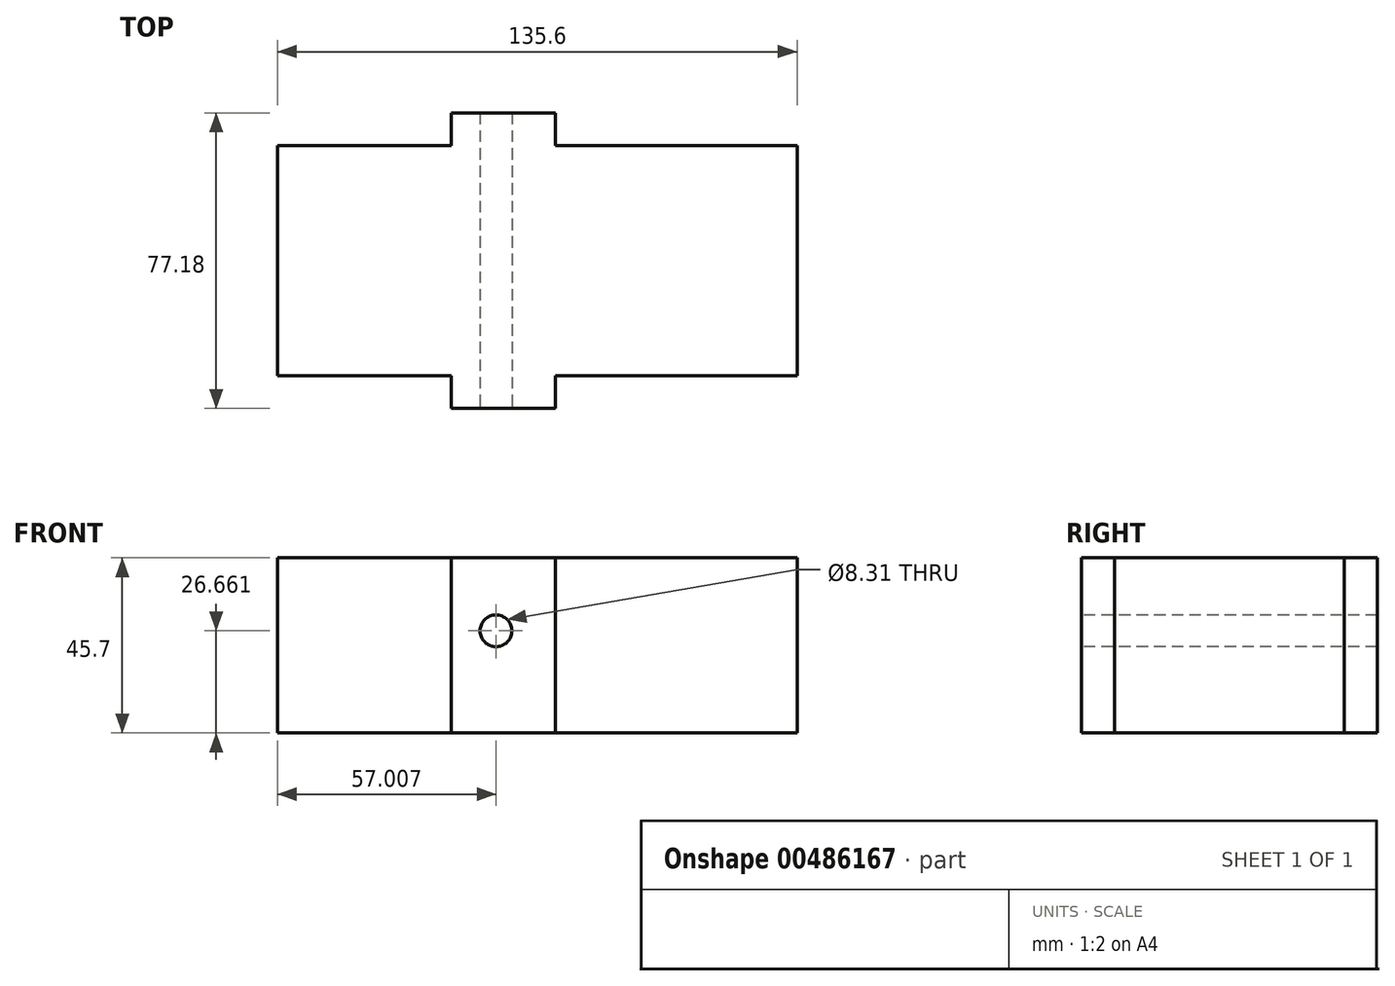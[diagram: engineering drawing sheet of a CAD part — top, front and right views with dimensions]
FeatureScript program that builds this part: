
annotation { "Feature Type Name" : "Feature", "Feature Type Description" : "" }
export const myFeature = defineFeature(function(context is Context, id is Id, definition is map)
    precondition{}
    {
        {
            var Q0;
            Q0=qCreatedBy(makeId("Top.planeOp"),FACE);
            var sketch = newSketch(context, id + "F0", { "sketchPlane" : qUnion([Q0])});
            skLineSegment(sketch, "E0.bottom", {"start": v(67.8, -30) * mm, "end": v(-67.8, -30) * mm});
            skLineSegment(sketch, "E0.top", {"start": v(67.8, 30) * mm, "end": v(-67.8, 30) * mm});
            skLineSegment(sketch, "E0.left", {"start": v(67.8, -30) * mm, "end": v(67.8, 30) * mm});
            skLineSegment(sketch, "E0.right", {"start": v(-67.8, -30) * mm, "end": v(-67.8, 30) * mm});
            skPoint(sketch, "E0.middle", {"position": v(0, 0) * mm});
            skLineSegment(sketch, "E1", {"start": v(-22.47, 30) * mm, "end": v(-22.47, 38.6) * mm});
            skLineSegment(sketch, "E2", {"start": v(-22.47, 38.6) * mm, "end": v(4.76, 38.6) * mm});
            skLineSegment(sketch, "E3", {"start": v(4.76, 38.6) * mm, "end": v(4.76, 30) * mm});
            skLineSegment(sketch, "E4.MirrorCS", {"start": v(-22.47, -30) * mm, "end": v(-22.47, -38.6) * mm});
            skLineSegment(sketch, "E5.MirrorCS", {"start": v(-22.47, -38.6) * mm, "end": v(4.76, -38.6) * mm});
            skLineSegment(sketch, "E6.MirrorCS", {"start": v(4.76, -38.6) * mm, "end": v(4.76, -30) * mm});
            skSolve(sketch);
        }
        {
            var Q0;
            {var subQ0=sQuery(id+"F0.wireOp",EDGE,"E0.left");Q0=makeQuery(id+"F0.imprint","IMPRINT",FACE,{"disambiguationData":[TD([[makeQuery(id+"F0.imprint","IMPRINT",EDGE,{"derivedFrom":subQ0}),1.0]])]});}
            var Q1;
            {var subQ0=sQuery(id+"F0.wireOp",EDGE,"E1");Q1=makeQuery(id+"F0.imprint","IMPRINT",FACE,{"disambiguationData":[TD([[makeQuery(id+"F0.imprint","IMPRINT",EDGE,{"derivedFrom":subQ0}),-1.0]])]});}
            var Q2;
            {var subQ0=sQuery(id+"F0.wireOp",EDGE,"E4.MirrorCS");Q2=makeQuery(id+"F0.imprint","IMPRINT",FACE,{"disambiguationData":[TD([[makeQuery(id+"F0.imprint","IMPRINT",EDGE,{"derivedFrom":subQ0}),1.0]])]});}
            extrude(context, id + "F1", {"entities" : qUnion([Q0, Q1, Q2]), "oppositeDirection" : true, "depth" : 45.7 * mm});
        }
        {
            var Q0;
            Q0=makeQuery(id+"F1.opExtrude","SWEPT_FACE",FACE,{"disambiguationData":[OSD([sQuery(id+"F0.wireOp",EDGE,"E5.MirrorCS")])]});
            var sketch = newSketch(context, id + "F2", { "sketchPlane" : qUnion([Q0])});
            skCircle(sketch, "E7", {"center": v(-10.8, -19.04) * mm, "radius": 4.15 * mm});
            skSolve(sketch);
        }
        {
            var Q0;
            Q0=makeQuery(id+"F2.imprint","IMPRINT",FACE,{"disambiguationData":[TD([[makeQuery(id+"F2.imprint","IMPRINT",EDGE,{"derivedFrom":sQuery(id+"F2.wireOp",EDGE,"E7")}),1.0]])]});
            extrude(context, id + "F3", {"entities" : qUnion([Q0]), "operationType" : NewBodyOperationType.REMOVE, "endBound" : BoundingType.THROUGH_ALL, "oppositeDirection" : true, "depth" : 25 * mm});
        }
    });
